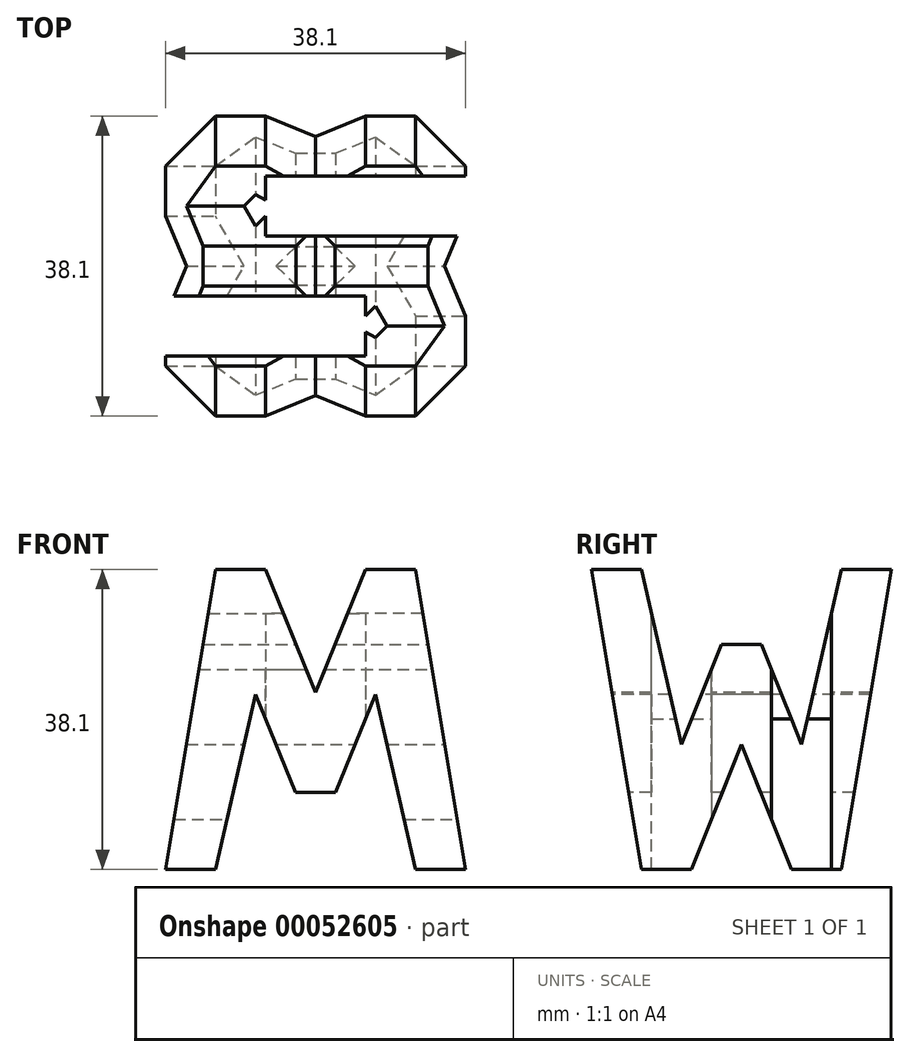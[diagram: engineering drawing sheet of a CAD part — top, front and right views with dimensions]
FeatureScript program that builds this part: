
annotation { "Feature Type Name" : "Feature", "Feature Type Description" : "" }
export const myFeature = defineFeature(function(context is Context, id is Id, definition is map)
    precondition{}
    {
        {
            var Q0;
            Q0=qCreatedBy(makeId("Front.planeOp"),FACE);
            var sketch = newSketch(context, id + "F0", { "sketchPlane" : qUnion([Q0])});
            skLineSegment(sketch, "E0", {"start": v(0, 0) * mm, "end": v(0, 38.1) * mm});
            skLineSegment(sketch, "E1", {"start": v(0, 38.1) * mm, "end": v(38.1, 38.1) * mm});
            skLineSegment(sketch, "E2", {"start": v(38.1, 38.1) * mm, "end": v(38.1, 0) * mm});
            skLineSegment(sketch, "E3", {"start": v(38.1, 0) * mm, "end": v(0, 0) * mm});
            skSolve(sketch);
        }
        {
            var Q0;
            Q0 = qSketchRegion(id + "F0", true);
            extrude(context, id + "F1", {"entities" : qUnion([Q0]), "depth" : 38.1 * mm});
        }
        {
            var Q0;
            Q0=qCreatedBy(makeId("Front.planeOp"),FACE);
            cPlane(context, id + "F2", {"entities" : qUnion([Q0]), "cplaneType" : CPlaneType.OFFSET, "offset" : 38.1 * mm, "width" : 152.4 * mm, "height" : 152.4 * mm});
        }
        {
            var Q0;
            Q0=qCreatedBy(makeId("Top.planeOp"),FACE);
            cPlane(context, id + "F3", {"entities" : qUnion([Q0]), "cplaneType" : CPlaneType.OFFSET, "offset" : 38.1 * mm, "width" : 152.4 * mm, "height" : 152.4 * mm});
        }
        {
            var Q0;
            Q0=makeQuery(id+"F1.opExtrude","SWEPT_FACE",FACE,{"disambiguationData":[OSD([sQuery(id+"F0.wireOp",EDGE,"E2")])]});
            var sketch = newSketch(context, id + "F4", { "sketchPlane" : qUnion([Q0])});
            skLineSegment(sketch, "E4", {"start": v(0, 38.1) * mm, "end": v(-6.35, 0) * mm});
            skLineSegment(sketch, "E5", {"start": v(-6.35, 38.1) * mm, "end": v(-11.43, 15.87) * mm});
            skLineSegment(sketch, "E6", {"start": v(-11.43, 15.87) * mm, "end": v(-16.5, 28.57) * mm});
            skLineSegment(sketch, "E7", {"start": v(-16.5, 28.57) * mm, "end": v(-21.59, 28.57) * mm});
            skLineSegment(sketch, "E8", {"start": v(-21.59, 28.57) * mm, "end": v(-26.67, 15.87) * mm});
            skLineSegment(sketch, "E9", {"start": v(-12.7, 0) * mm, "end": v(-19.05, 15.88) * mm});
            skLineSegment(sketch, "E10", {"start": v(-19.05, 15.88) * mm, "end": v(-25.4, 0) * mm});
            skLineSegment(sketch, "E11", {"start": v(-38.1, 38.1) * mm, "end": v(-31.75, 0) * mm});
            skLineSegment(sketch, "E12", {"start": v(-31.75, 38.1) * mm, "end": v(-26.67, 15.87) * mm});
            skLineSegment(sketch, "E13.bottom", {"start": v(0, 0) * mm, "end": v(-38.1, 0) * mm});
            skLineSegment(sketch, "E13.top", {"start": v(0, 38.1) * mm, "end": v(-38.1, 38.1) * mm});
            skLineSegment(sketch, "E13.left", {"start": v(0, 0) * mm, "end": v(0, 38.1) * mm});
            skLineSegment(sketch, "E13.right", {"start": v(-38.1, 0) * mm, "end": v(-38.1, 38.1) * mm});
            skSolve(sketch);
        }
        {
            var Q0;
            {var subQ0=sQuery(id+"F4.wireOp",EDGE,"E11");Q0=makeQuery(id+"F4.imprint","IMPRINT",FACE,{"disambiguationData":[TD([[makeQuery(id+"F4.imprint","IMPRINT",EDGE,{"derivedFrom":subQ0}),-1.0]])]});}
            var Q1;
            {var subQ0=sQuery(id+"F4.wireOp",EDGE,"E5");Q1=makeQuery(id+"F4.imprint","IMPRINT",FACE,{"disambiguationData":[TD([[makeQuery(id+"F4.imprint","IMPRINT",EDGE,{"derivedFrom":subQ0}),-1.0]])]});}
            var Q2;
            {var subQ0=sQuery(id+"F4.wireOp",EDGE,"E4");Q2=makeQuery(id+"F4.imprint","IMPRINT",FACE,{"disambiguationData":[TD([[makeQuery(id+"F4.imprint","IMPRINT",EDGE,{"derivedFrom":subQ0}),1.0]])]});}
            var Q3;
            {var subQ0=sQuery(id+"F4.wireOp",EDGE,"E9");Q3=makeQuery(id+"F4.imprint","IMPRINT",FACE,{"disambiguationData":[TD([[makeQuery(id+"F4.imprint","IMPRINT",EDGE,{"derivedFrom":subQ0}),1.0]])]});}
            extrude(context, id + "F5", {"entities" : qUnion([Q0, Q1, Q2, Q3]), "operationType" : NewBodyOperationType.REMOVE, "oppositeDirection" : true, "depth" : 38.1 * mm});
        }
        {
            var Q0;
            Q0=qCreatedBy(id+"F2.planeOp",FACE);
            var sketch = newSketch(context, id + "F6", { "sketchPlane" : qUnion([Q0])});
            skLineSegment(sketch, "E14.bottom", {"start": v(0, 0) * mm, "end": v(38.1, 0) * mm});
            skLineSegment(sketch, "E14.top", {"start": v(0, 38.1) * mm, "end": v(38.1, 38.1) * mm});
            skLineSegment(sketch, "E14.left", {"start": v(0, 0) * mm, "end": v(0, 38.1) * mm});
            skLineSegment(sketch, "E14.right", {"start": v(38.1, 0) * mm, "end": v(38.1, 38.1) * mm});
            skLineSegment(sketch, "E15", {"start": v(0, 0) * mm, "end": v(6.35, 38.1) * mm});
            skLineSegment(sketch, "E16", {"start": v(6.35, 0) * mm, "end": v(11.43, 22.23) * mm});
            skLineSegment(sketch, "E17", {"start": v(11.43, 22.23) * mm, "end": v(16.51, 9.8) * mm});
            skLineSegment(sketch, "E18", {"start": v(16.51, 9.8) * mm, "end": v(21.6, 9.8) * mm});
            skLineSegment(sketch, "E19", {"start": v(21.6, 9.8) * mm, "end": v(26.67, 22.22) * mm});
            skLineSegment(sketch, "E20", {"start": v(26.67, 22.23) * mm, "end": v(31.75, 0) * mm});
            skLineSegment(sketch, "E21", {"start": v(38.1, 0) * mm, "end": v(31.75, 38.1) * mm});
            skLineSegment(sketch, "E22", {"start": v(12.7, 38.1) * mm, "end": v(19.05, 22.5) * mm});
            skLineSegment(sketch, "E23", {"start": v(19.05, 22.5) * mm, "end": v(25.4, 38.1) * mm});
            skSolve(sketch);
        }
        {
            var Q0;
            {var subQ0=sQuery(id+"F6.wireOp",EDGE,"E14.left");Q0=makeQuery(id+"F6.imprint","IMPRINT",FACE,{"disambiguationData":[TD([[makeQuery(id+"F6.imprint","IMPRINT",EDGE,{"derivedFrom":subQ0}),-1.0]])]});}
            var Q1;
            {var subQ0=sQuery(id+"F6.wireOp",EDGE,"E22");Q1=makeQuery(id+"F6.imprint","IMPRINT",FACE,{"disambiguationData":[TD([[makeQuery(id+"F6.imprint","IMPRINT",EDGE,{"derivedFrom":subQ0}),1.0]])]});}
            var Q2;
            {var subQ0=sQuery(id+"F6.wireOp",EDGE,"E14.right");Q2=makeQuery(id+"F6.imprint","IMPRINT",FACE,{"disambiguationData":[TD([[makeQuery(id+"F6.imprint","IMPRINT",EDGE,{"derivedFrom":subQ0}),1.0]])]});}
            var Q3;
            {var subQ0=sQuery(id+"F6.wireOp",EDGE,"E16");Q3=makeQuery(id+"F6.imprint","IMPRINT",FACE,{"disambiguationData":[TD([[makeQuery(id+"F6.imprint","IMPRINT",EDGE,{"derivedFrom":subQ0}),-1.0]])]});}
            extrude(context, id + "F7", {"entities" : qUnion([Q0, Q1, Q2, Q3]), "operationType" : NewBodyOperationType.REMOVE, "oppositeDirection" : true, "depth" : 38.1 * mm});
        }
        {
            var Q0;
            Q0=qCreatedBy(id+"F3.planeOp",FACE);
            var sketch = newSketch(context, id + "F8", { "sketchPlane" : qUnion([Q0])});
            skLineSegment(sketch, "E24.bottom", {"start": v(0, 0) * mm, "end": v(38.1, 0) * mm});
            skLineSegment(sketch, "E24.top", {"start": v(0, -38.1) * mm, "end": v(38.1, -38.1) * mm});
            skLineSegment(sketch, "E24.left", {"start": v(0, 0) * mm, "end": v(0, -38.1) * mm});
            skLineSegment(sketch, "E24.right", {"start": v(38.1, 0) * mm, "end": v(38.1, -38.1) * mm});
            skLineSegment(sketch, "E25", {"start": v(38.1, -7.62) * mm, "end": v(12.7, -7.62) * mm});
            skLineSegment(sketch, "E26", {"start": v(12.7, -7.62) * mm, "end": v(12.7, -15.24) * mm});
            skLineSegment(sketch, "E27", {"start": v(12.7, -15.24) * mm, "end": v(38.1, -15.24) * mm});
            skLineSegment(sketch, "E28", {"start": v(0, -22.86) * mm, "end": v(25.4, -22.86) * mm});
            skLineSegment(sketch, "E29", {"start": v(25.4, -22.86) * mm, "end": v(25.4, -30.48) * mm});
            skLineSegment(sketch, "E30", {"start": v(25.4, -30.48) * mm, "end": v(0, -30.48) * mm});
            skSolve(sketch);
        }
        {
            var Q0;
            {var subQ0=sQuery(id+"F8.wireOp",EDGE,"E25");Q0=makeQuery(id+"F8.imprint","IMPRINT",FACE,{"disambiguationData":[TD([[makeQuery(id+"F8.imprint","IMPRINT",EDGE,{"derivedFrom":subQ0}),1.0]])]});}
            var Q1;
            {var subQ0=sQuery(id+"F8.wireOp",EDGE,"E28");Q1=makeQuery(id+"F8.imprint","IMPRINT",FACE,{"disambiguationData":[TD([[makeQuery(id+"F8.imprint","IMPRINT",EDGE,{"derivedFrom":subQ0}),-1.0]])]});}
            extrude(context, id + "F9", {"entities" : qUnion([Q0, Q1]), "operationType" : NewBodyOperationType.REMOVE, "oppositeDirection" : true, "depth" : 38.1 * mm});
        }
    });
